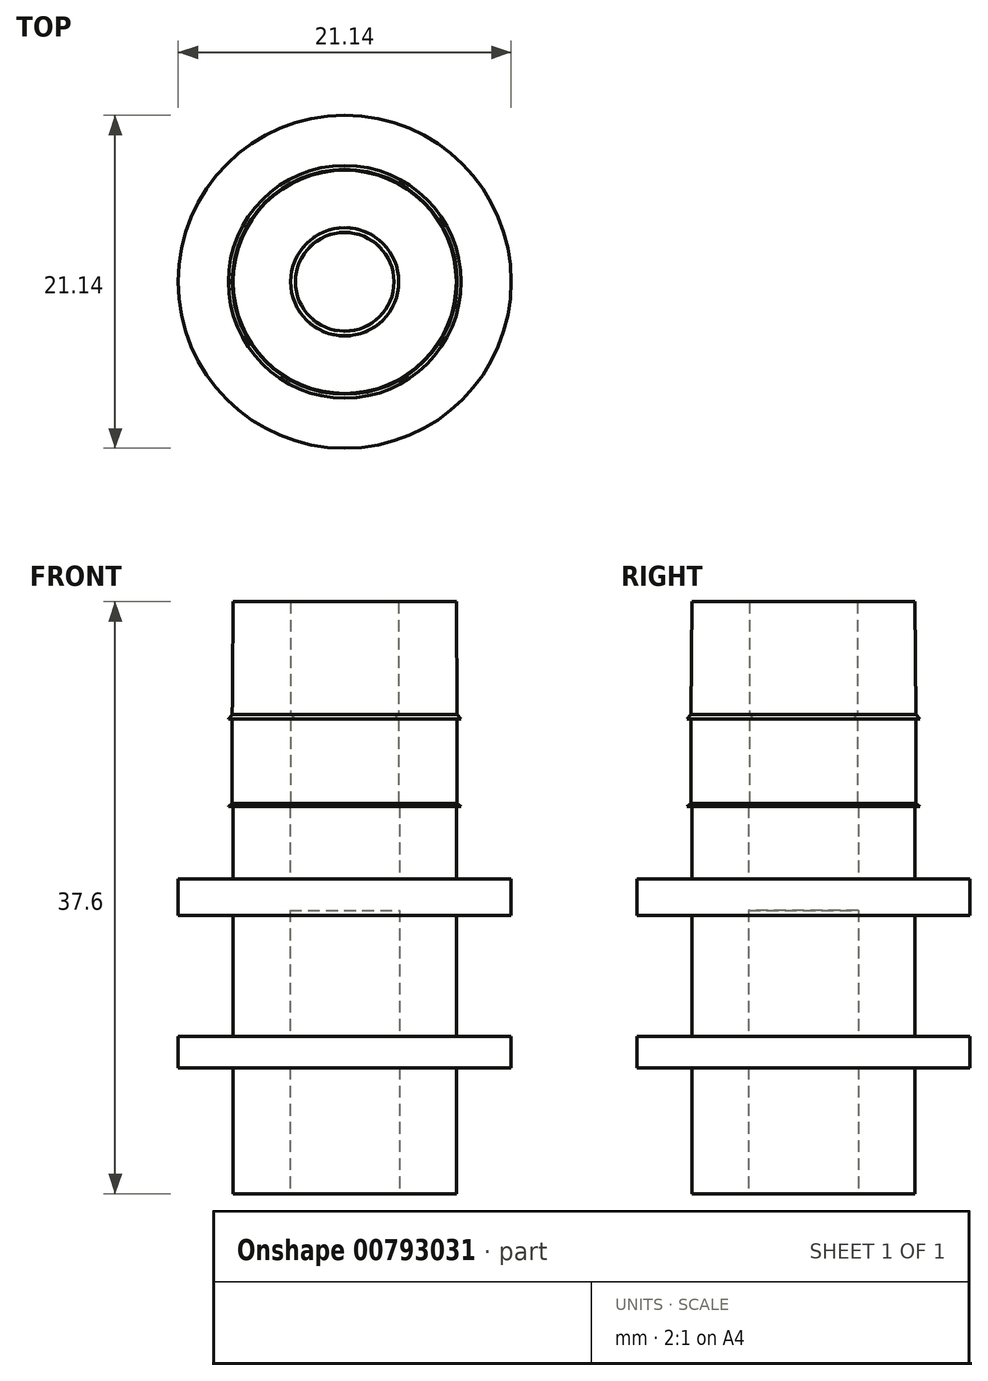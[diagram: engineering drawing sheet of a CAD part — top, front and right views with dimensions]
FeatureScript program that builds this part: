
annotation { "Feature Type Name" : "Feature", "Feature Type Description" : "" }
export const myFeature = defineFeature(function(context is Context, id is Id, definition is map)
    precondition{}
    {
        {
            var Q0;
            Q0=qCreatedBy(makeId("Front.planeOp"),FACE);
            var sketch = newSketch(context, id + "F0", { "sketchPlane" : qUnion([Q0])});
            skLineSegment(sketch, "E0", {"start": v(-7.09, 0) * mm, "end": v(-7.09, 8) * mm});
            skLineSegment(sketch, "E1", {"start": v(-7.09, 8) * mm, "end": v(-10.57, 8) * mm});
            skLineSegment(sketch, "E2", {"start": v(-10.57, 10) * mm, "end": v(-7.09, 10) * mm});
            skLineSegment(sketch, "E3", {"start": v(-7.09, 10) * mm, "end": v(-7.09, 17.67) * mm});
            skLineSegment(sketch, "E4", {"start": v(-7.09, 20) * mm, "end": v(-10.57, 20) * mm});
            skLineSegment(sketch, "E5", {"start": v(-3.49, 0) * mm, "end": v(-3.49, 8) * mm});
            skLineSegment(sketch, "E6", {"start": v(-3.49, 8) * mm, "end": v(0, 8) * mm});
            skLineSegment(sketch, "E7", {"start": v(0, 8) * mm, "end": v(0, 10) * mm});
            skLineSegment(sketch, "E8", {"start": v(0, 10) * mm, "end": v(-3.49, 10) * mm});
            skLineSegment(sketch, "E9", {"start": v(-3.49, 10) * mm, "end": v(-3.49, 18) * mm});
            skLineSegment(sketch, "E10", {"start": v(-3.49, 20) * mm, "end": v(0, 20) * mm});
            skLineSegment(sketch, "E11", {"start": v(0, 18) * mm, "end": v(0, 20) * mm});
            skLineSegment(sketch, "E12", {"start": v(-10.57, 17.67) * mm, "end": v(-7.09, 17.67) * mm});
            skLineSegment(sketch, "E13", {"start": v(0, 18) * mm, "end": v(-3.49, 18) * mm});
            skLineSegment(sketch, "E14", {"start": v(-7.09, 20) * mm, "end": v(-7.09, 24.6) * mm});
            skLineSegment(sketch, "E15", {"start": v(-3.49, 20) * mm, "end": v(-3.49, 24.6) * mm});
            skLineSegment(sketch, "E16", {"start": v(-3.43, 37.6) * mm, "end": v(-7.09, 37.6) * mm});
            skLineSegment(sketch, "E17", {"start": v(-3.49, 0) * mm, "end": v(-7.09, 0) * mm});
            skLineSegment(sketch, "E18", {"start": v(-7.14, 24.77) * mm, "end": v(-7.39, 24.6) * mm});
            skLineSegment(sketch, "E19", {"start": v(-7.39, 24.6) * mm, "end": v(-7.09, 24.6) * mm});
            skPoint(sketch, "E20.orphan", {"position": v(-7.09, 20.6) * mm});
            skPoint(sketch, "E21.trimOffspring.start.orphan", {"position": v(-7.09, 21.58) * mm});
            skPoint(sketch, "E22.orphan", {"position": v(-3.49, 19.76) * mm});
            skPoint(sketch, "E23.orphan", {"position": v(-3.49, 20.6) * mm});
            skLineSegment(sketch, "E24", {"start": v(-3.43, 24.77) * mm, "end": v(-3.19, 24.6) * mm});
            skLineSegment(sketch, "E25", {"start": v(-3.19, 24.6) * mm, "end": v(-3.49, 24.6) * mm});
            skLineSegment(sketch, "E26", {"start": v(-7.14, 24.77) * mm, "end": v(-7.14, 30.15) * mm});
            skLineSegment(sketch, "E27", {"start": v(-7.14, 30.15) * mm, "end": v(-7.39, 30.15) * mm});
            skLineSegment(sketch, "E28", {"start": v(-3.43, 24.77) * mm, "end": v(-3.43, 30.15) * mm});
            skLineSegment(sketch, "E29", {"start": v(-3.43, 30.15) * mm, "end": v(-3.13, 30.15) * mm});
            skLineSegment(sketch, "E30", {"start": v(-7.39, 30.15) * mm, "end": v(-7.14, 30.43) * mm});
            skLineSegment(sketch, "E31", {"start": v(-7.14, 30.43) * mm, "end": v(-7.09, 37.6) * mm});
            skLineSegment(sketch, "E32", {"start": v(-3.13, 30.15) * mm, "end": v(-3.43, 30.43) * mm});
            skLineSegment(sketch, "E33", {"start": v(-3.43, 30.43) * mm, "end": v(-3.43, 37.6) * mm});
            skLineSegment(sketch, "E34", {"start": v(-10.57, 10) * mm, "end": v(-10.57, 8) * mm});
            skLineSegment(sketch, "E35", {"start": v(-10.57, 17.67) * mm, "end": v(-10.57, 20) * mm});
            skSolve(sketch);
        }
        {
            var Q0;
            Q0 = qSketchRegion(id + "F0", true);
            var Q1;
            Q1=sQuery(id+"F0.wireOp",EDGE,"E11");
            revolve(context, id + "F1", {"surfaceOperationType" : NewSurfaceOperationType.NEW, "entities" : qUnion([Q0]), "axis" : qUnion([Q1]), "revolveType" : RevolveType.FULL});
        }
    });
